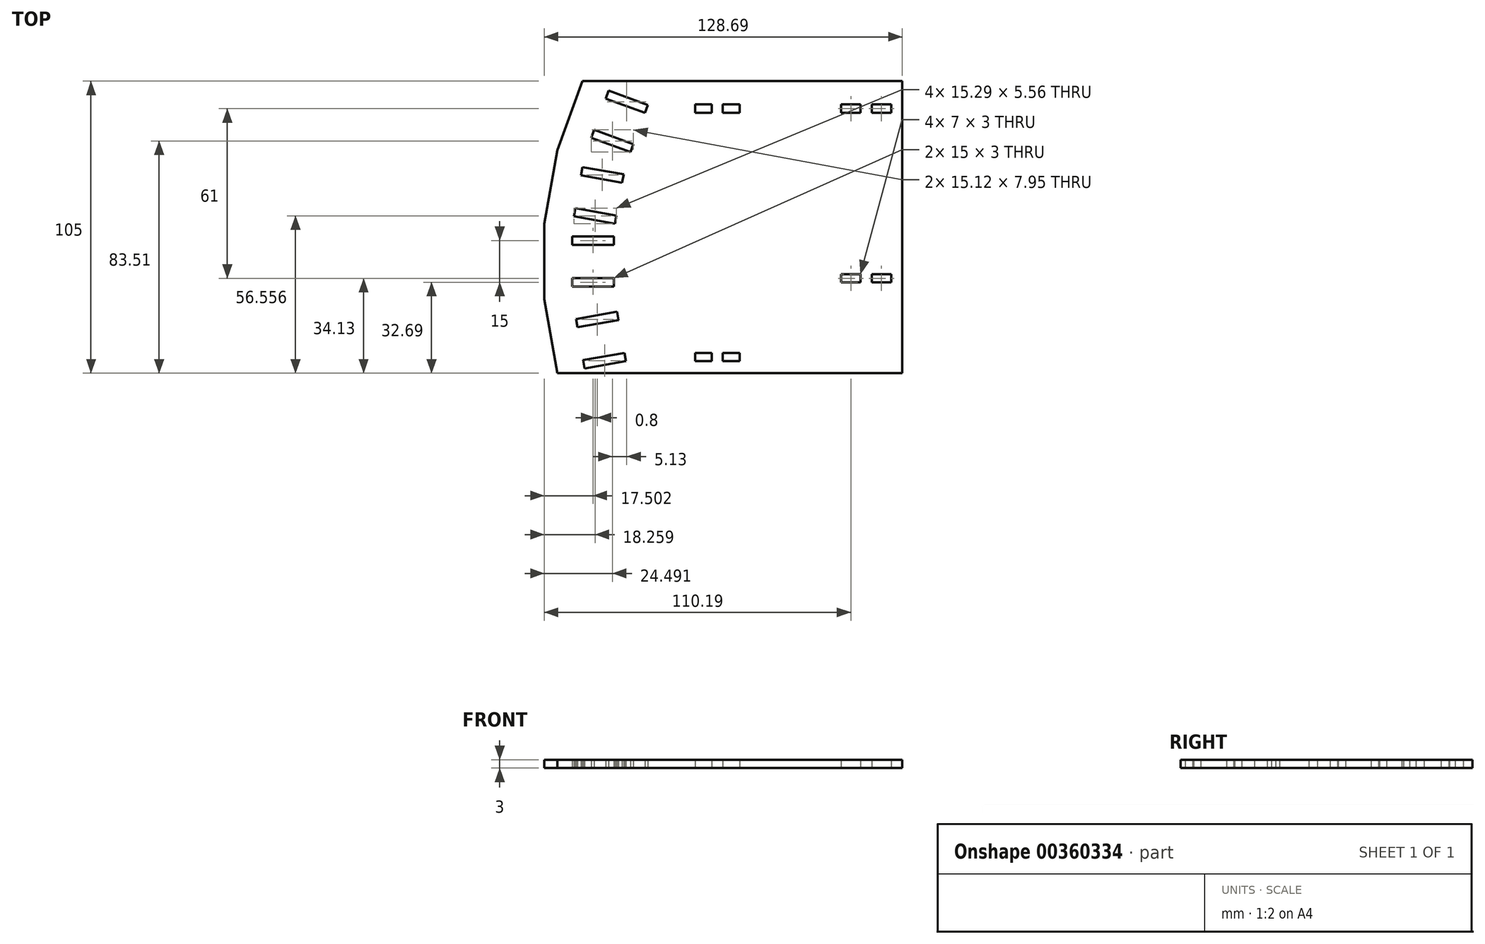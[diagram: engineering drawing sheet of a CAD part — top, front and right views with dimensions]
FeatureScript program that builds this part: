
annotation { "Feature Type Name" : "Feature", "Feature Type Description" : "" }
export const myFeature = defineFeature(function(context is Context, id is Id, definition is map)
    precondition{}
    {
        {
            var Q0;
            Q0=qCreatedBy(makeId("Top.planeOp"),FACE);
            var sketch = newSketch(context, id + "F0", { "sketchPlane" : qUnion([Q0])});
            skLineSegment(sketch, "E0.bottom", {"start": v(49.5, -52.5) * mm, "end": v(-49.5, -52.5) * mm});
            skLineSegment(sketch, "E0.left", {"start": v(49.5, -52.5) * mm, "end": v(49.5, 52.5) * mm, "construction": true});
            skPoint(sketch, "E0.middle", {"position": v(0, 0) * mm});
            skLineSegment(sketch, "E1", {"start": v(-40.5, 52.5) * mm, "end": v(-49.54, 27.67) * mm});
            skLineSegment(sketch, "E2", {"start": v(-54.19, -25.91) * mm, "end": v(-49.5, -52.5) * mm});
            skLineSegment(sketch, "E3", {"start": v(-40.5, 52.5) * mm, "end": v(49.5, 52.5) * mm});
            skLineSegment(sketch, "E4", {"start": v(-49.54, 27.67) * mm, "end": v(-54.19, 1.29) * mm});
            skLineSegment(sketch, "E5", {"start": v(-54.19, 1.29) * mm, "end": v(-54.19, -25.91) * mm});
            skPoint(sketch, "E6.startSnap0", {"position": v(-51.06, -43.64) * mm});
            skLineSegment(sketch, "E7", {"start": v(-32.13, 46.26) * mm, "end": v(-31.1, 49.08) * mm});
            skLineSegment(sketch, "E8", {"start": v(-31.1, 49.08) * mm, "end": v(-17, 43.95) * mm});
            skLineSegment(sketch, "E9", {"start": v(-17, 43.95) * mm, "end": v(-18.03, 41.13) * mm});
            skLineSegment(sketch, "E10", {"start": v(-18.03, 41.13) * mm, "end": v(-32.13, 46.26) * mm});
            skLineSegment(sketch, "E11", {"start": v(-43.58, 44.04) * mm, "end": v(77.43, 0) * mm, "construction": true});
            skLineSegment(sketch, "E12", {"start": v(-51.86, 14.48) * mm, "end": v(30.26, 0) * mm, "construction": true});
            skLineSegment(sketch, "E13", {"start": v(-54.19, -12.31) * mm, "end": v(0, -12.31) * mm, "construction": true});
            skLineSegment(sketch, "E14", {"start": v(-51.06, -43.64) * mm, "end": v(0, -34.63) * mm, "construction": true});
            skLineSegment(sketch, "E15", {"start": v(-40.45, 21.6) * mm, "end": v(-40.97, 18.65) * mm});
            skLineSegment(sketch, "E16", {"start": v(-40.97, 18.65) * mm, "end": v(-26.2, 16.05) * mm});
            skLineSegment(sketch, "E17", {"start": v(-26.2, 16.05) * mm, "end": v(-25.68, 19) * mm});
            skLineSegment(sketch, "E18", {"start": v(-25.68, 19) * mm, "end": v(-40.45, 21.6) * mm});
            skLineSegment(sketch, "E19", {"start": v(-42.26, -36) * mm, "end": v(-27.48, -33.39) * mm});
            skLineSegment(sketch, "E20", {"start": v(-27.48, -33.39) * mm, "end": v(-28, -30.43) * mm});
            skLineSegment(sketch, "E21", {"start": v(-28, -30.43) * mm, "end": v(-42.78, -33.04) * mm});
            skLineSegment(sketch, "E22", {"start": v(-42.78, -33.04) * mm, "end": v(-42.26, -36) * mm});
            skLineSegment(sketch, "E23.bottom", {"start": v(-44.19, -18.31) * mm, "end": v(-29.19, -18.31) * mm});
            skLineSegment(sketch, "E23.top", {"start": v(-44.19, -21.31) * mm, "end": v(-29.19, -21.31) * mm});
            skLineSegment(sketch, "E23.left", {"start": v(-44.19, -18.31) * mm, "end": v(-44.19, -21.31) * mm});
            skLineSegment(sketch, "E23.right", {"start": v(-29.19, -18.31) * mm, "end": v(-29.19, -21.31) * mm});
            skLineSegment(sketch, "E24.MirrorCS", {"start": v(-23.16, 27.04) * mm, "end": v(-22.14, 29.85) * mm});
            skLineSegment(sketch, "E25.MirrorCS", {"start": v(-37.26, 32.17) * mm, "end": v(-23.16, 27.04) * mm});
            skLineSegment(sketch, "E26.MirrorCS", {"start": v(-36.23, 34.98) * mm, "end": v(-37.26, 32.17) * mm});
            skLineSegment(sketch, "E27.MirrorCS", {"start": v(-22.14, 29.85) * mm, "end": v(-36.23, 34.98) * mm});
            skLineSegment(sketch, "E28.MirrorCS", {"start": v(-28.28, 4.23) * mm, "end": v(-28.8, 1.28) * mm});
            skLineSegment(sketch, "E29.MirrorCS", {"start": v(-28.8, 1.28) * mm, "end": v(-43.58, 3.88) * mm});
            skLineSegment(sketch, "E30.MirrorCS", {"start": v(-43.58, 3.88) * mm, "end": v(-43.06, 6.84) * mm});
            skLineSegment(sketch, "E31.MirrorCS", {"start": v(-43.06, 6.84) * mm, "end": v(-28.28, 4.23) * mm});
            skLineSegment(sketch, "E32.MirrorCS", {"start": v(-29.19, -6.31) * mm, "end": v(-29.19, -3.31) * mm});
            skLineSegment(sketch, "E33.MirrorCS", {"start": v(-44.19, -3.31) * mm, "end": v(-29.19, -3.31) * mm});
            skLineSegment(sketch, "E34.MirrorCS", {"start": v(-44.19, -6.31) * mm, "end": v(-44.19, -3.31) * mm});
            skLineSegment(sketch, "E35.MirrorCS", {"start": v(-44.19, -6.31) * mm, "end": v(-29.19, -6.31) * mm});
            skLineSegment(sketch, "E36.MirrorCS", {"start": v(-25.4, -45.2) * mm, "end": v(-24.88, -48.16) * mm});
            skLineSegment(sketch, "E37.MirrorCS", {"start": v(-24.88, -48.16) * mm, "end": v(-39.65, -50.76) * mm});
            skLineSegment(sketch, "E38.MirrorCS", {"start": v(-40.17, -47.8) * mm, "end": v(-25.4, -45.2) * mm});
            skLineSegment(sketch, "E39", {"start": v(-40.17, -47.8) * mm, "end": v(-39.65, -50.76) * mm});
            skLineSegment(sketch, "E40", {"start": v(-39.65, -50.76) * mm, "end": v(-49.5, -52.5) * mm, "construction": true});
            skLineSegment(sketch, "E41", {"start": v(-31.1, 49.08) * mm, "end": v(-40.5, 52.5) * mm, "construction": true});
            skLineSegment(sketch, "E42.bottom", {"start": v(0, 44.13) * mm, "end": v(6, 44.13) * mm});
            skLineSegment(sketch, "E42.top", {"start": v(0, 41.13) * mm, "end": v(6, 41.13) * mm});
            skLineSegment(sketch, "E42.left", {"start": v(0, 44.13) * mm, "end": v(0, 41.13) * mm});
            skLineSegment(sketch, "E42.right", {"start": v(6, 44.13) * mm, "end": v(6, 41.13) * mm});
            skLineSegment(sketch, "E43.bottom", {"start": v(0, -45.2) * mm, "end": v(6, -45.2) * mm});
            skLineSegment(sketch, "E43.top", {"start": v(0, -48.2) * mm, "end": v(6, -48.2) * mm});
            skLineSegment(sketch, "E43.left", {"start": v(0, -45.2) * mm, "end": v(0, -48.2) * mm});
            skLineSegment(sketch, "E43.right", {"start": v(6, -45.2) * mm, "end": v(6, -48.2) * mm});
            skLineSegment(sketch, "E44", {"start": v(-25.4, -45.2) * mm, "end": v(0, -45.2) * mm, "construction": true});
            skLineSegment(sketch, "E45", {"start": v(-18.03, 41.13) * mm, "end": v(0, 41.13) * mm, "construction": true});
            skLineSegment(sketch, "E46.bottom", {"start": v(52.5, 44.13) * mm, "end": v(59.5, 44.13) * mm});
            skLineSegment(sketch, "E46.top", {"start": v(52.5, 41.13) * mm, "end": v(59.5, 41.13) * mm});
            skLineSegment(sketch, "E46.left", {"start": v(52.5, 44.13) * mm, "end": v(52.5, 41.13) * mm});
            skLineSegment(sketch, "E46.right", {"start": v(59.5, 44.13) * mm, "end": v(59.5, 41.13) * mm});
            skLineSegment(sketch, "E47.bottom", {"start": v(63.5, 44.13) * mm, "end": v(70.5, 44.13) * mm});
            skLineSegment(sketch, "E47.top", {"start": v(63.5, 41.13) * mm, "end": v(70.5, 41.13) * mm});
            skLineSegment(sketch, "E47.left", {"start": v(63.5, 44.13) * mm, "end": v(63.5, 41.13) * mm});
            skLineSegment(sketch, "E47.right", {"start": v(70.5, 44.13) * mm, "end": v(70.5, 41.13) * mm});
            skLineSegment(sketch, "E48.bottom", {"start": v(52.5, -16.87) * mm, "end": v(59.5, -16.87) * mm});
            skLineSegment(sketch, "E48.top", {"start": v(52.5, -19.87) * mm, "end": v(59.5, -19.87) * mm});
            skLineSegment(sketch, "E48.left", {"start": v(52.5, -16.87) * mm, "end": v(52.5, -19.87) * mm});
            skLineSegment(sketch, "E48.right", {"start": v(59.5, -16.87) * mm, "end": v(59.5, -19.87) * mm});
            skLineSegment(sketch, "E49.bottom", {"start": v(63.5, -16.87) * mm, "end": v(70.5, -16.87) * mm});
            skLineSegment(sketch, "E49.top", {"start": v(63.5, -19.87) * mm, "end": v(70.5, -19.87) * mm});
            skLineSegment(sketch, "E49.left", {"start": v(63.5, -16.87) * mm, "end": v(63.5, -19.87) * mm});
            skLineSegment(sketch, "E49.right", {"start": v(70.5, -16.87) * mm, "end": v(70.5, -19.87) * mm});
            skLineSegment(sketch, "E50", {"start": v(59.5, -16.87) * mm, "end": v(63.5, -16.87) * mm, "construction": true});
            skLineSegment(sketch, "E51", {"start": v(59.5, -19.87) * mm, "end": v(63.5, -19.87) * mm, "construction": true});
            skLineSegment(sketch, "E52.bottom", {"start": v(10, 44.13) * mm, "end": v(16, 44.13) * mm});
            skLineSegment(sketch, "E52.top", {"start": v(10, 41.13) * mm, "end": v(16, 41.13) * mm});
            skLineSegment(sketch, "E52.left", {"start": v(10, 44.13) * mm, "end": v(10, 41.13) * mm});
            skLineSegment(sketch, "E52.right", {"start": v(16, 44.13) * mm, "end": v(16, 41.13) * mm});
            skLineSegment(sketch, "E53.bottom", {"start": v(10, -45.2) * mm, "end": v(16, -45.2) * mm});
            skLineSegment(sketch, "E53.top", {"start": v(10, -48.2) * mm, "end": v(16, -48.2) * mm});
            skLineSegment(sketch, "E53.left", {"start": v(10, -45.2) * mm, "end": v(10, -48.2) * mm});
            skLineSegment(sketch, "E53.right", {"start": v(16, -45.2) * mm, "end": v(16, -48.2) * mm});
            skLineSegment(sketch, "E54", {"start": v(49.5, 52.5) * mm, "end": v(74.5, 52.5) * mm});
            skLineSegment(sketch, "E55", {"start": v(74.5, 52.5) * mm, "end": v(74.5, -52.5) * mm});
            skLineSegment(sketch, "E56", {"start": v(74.5, -52.5) * mm, "end": v(49.5, -52.5) * mm});
            skLineSegment(sketch, "E57", {"start": v(6, 44.13) * mm, "end": v(10, 44.13) * mm, "construction": true});
            skLineSegment(sketch, "E58", {"start": v(59.5, 44.13) * mm, "end": v(63.5, 44.13) * mm, "construction": true});
            skLineSegment(sketch, "E59", {"start": v(61.5, 44.13) * mm, "end": v(8, 44.13) * mm, "construction": true});
            skSolve(sketch);
        }
        {
            var Q0;
            Q0 = qSketchRegion(id + "F0", true);
            extrude(context, id + "F1", {"entities" : qUnion([Q0]), "depth" : 3 * mm});
        }
    });
